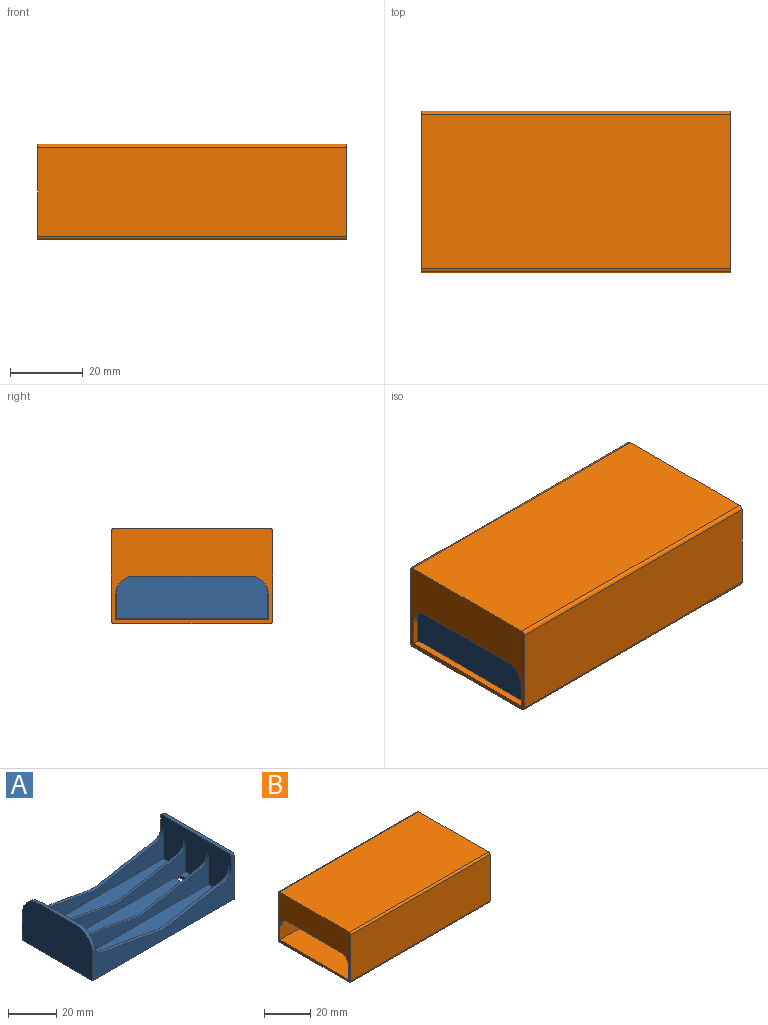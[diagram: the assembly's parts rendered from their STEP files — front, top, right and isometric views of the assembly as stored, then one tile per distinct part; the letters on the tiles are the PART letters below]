
ASSEMBLY  parts=2 mates=1
PART A: 45 faces, bbox 83.2x41.6x23.6 mm
  f0: plane 12x3.4mm, normal (0,0,1), area 40.8mm2, adj f6,f7,f11,f43
  f1: plane 83.2x22.6mm, normal (0,1,0), area 780.8mm2, adj f2,f11,f12,f17,f22,f23,f27,f30
  f2: plane 41.6x23.6mm, normal (-1,0,0), area 938.8mm2, adj f1,f3,f17,f18,f27,f28
  f3: plane 83.2x22.6mm, normal (0,-1,0), area 780.8mm2, adj f2,f11,f12,f17,f19,f26,f28,f29
  f4: plane 80x15mm, normal (0,1,0), area 595.9mm2, adj f9,f11,f16,f19,f26,f34,f35,f36
  f5: plane 80x15mm, normal (0,-1,0), area 595.9mm2, adj f9,f11,f16,f20,f24,f33,f37,f38
  f6: plane 80x16.6mm, normal (0,1,0), area 600.7mm2, adj f0,f9,f11,f15,f17,f20,f24,f33
  f7: plane 80x16.6mm, normal (0,-1,0), area 600.7mm2, adj f0,f9,f11,f15,f17,f21,f25,f32
  f8: plane 80x15mm, normal (0,1,0), area 595.9mm2, adj f9,f11,f14,f21,f25,f32,f39,f40
  f9: plane 40.68x22mm, normal (1,0,0), area 789.2mm2, adj f4,f5,f6,f7,f8,f10,f14,f15
  f10: plane 80x15mm, normal (0,-1,0), area 595.9mm2, adj f9,f11,f14,f22,f23,f31,f41,f42
  f11: plane 41.6x22mm, normal (-1,0,0), area 830.8mm2, adj f0,f1,f3,f4,f5,f6,f7,f8
  f12: plane 41.6x23.6mm, normal (1,0,0), area 981.3mm2, adj f1,f3,f13,f17,f29,f30
  f13: plane 39.6x1.6mm, normal (0,0,1), area 63.4mm2, adj f11,f12,f29,f30
  f14: plane 80x12mm, normal (0,0,1), area 960mm2, adj f8,f9,f10,f11
  f15: plane 73.6x12mm, normal (0,0,1), area 883.2mm2, adj f6,f7,f9,f44
  f16: plane 80x12mm, normal (0,0,1), area 960mm2, adj f4,f5,f9,f11
  f17: plane 83.2x41.6mm, normal (0,0,-1), area 3425.1mm2, adj f1,f2,f3,f6,f7,f12,f43,f44
  f18: plane 21.6x1.6mm, normal (0,0,1), area 34.6mm2, adj f2,f9,f27,f28
  f19: cylinder r=5mm len=4.94mm, axis (0,1,0), area 10.9mm2, adj f3,f4,f9,f28,f35
  f20: cylinder r=5mm len=4.94mm, axis (0,1,0), area 8.5mm2, adj f5,f6,f9,f37
  f21: cylinder r=5mm len=4.94mm, axis (0,1,0), area 8.5mm2, adj f7,f8,f9,f39
  f22: cylinder r=5mm len=4.94mm, axis (0,1,0), area 10.9mm2, adj f1,f9,f10,f27,f41
  f23: cylinder r=5mm len=4.94mm, axis (0,-1,0), area 11.3mm2, adj f1,f10,f11,f42
  f24: cylinder r=5mm len=4.94mm, axis (0,1,0), area 8.5mm2, adj f5,f6,f11,f38
  f25: cylinder r=5mm len=4.94mm, axis (0,1,0), area 8.5mm2, adj f7,f8,f11,f40
  f26: cylinder r=5mm len=4.94mm, axis (0,1,0), area 11.3mm2, adj f3,f4,f11,f36
  f27: cylinder r=10mm len=10mm, axis (1,0,0), area 26.1mm2, adj f1,f2,f9,f18,f22
  f28: cylinder r=10mm len=10mm, axis (-1,0,0), area 26.1mm2, adj f2,f3,f9,f18,f19
  f29: cylinder r=1mm len=1.6mm, axis (-1,0,0), area 2.5mm2, adj f3,f11,f12,f13
  f30: cylinder r=1mm len=1.6mm, axis (1,0,0), area 2.5mm2, adj f1,f11,f12,f13
  f31: cylinder r=21.24mm len=8.25mm, axis (0,-1,0), area 13.3mm2, adj f1,f10,f41,f42
  f32: cylinder r=21.24mm len=8.25mm, axis (0,-1,0), area 10mm2, adj f7,f8,f39,f40
  f33: cylinder r=21.24mm len=8.25mm, axis (0,-1,0), area 10mm2, adj f5,f6,f37,f38
  f34: cylinder r=21.24mm len=8.25mm, axis (0,-1,0), area 13.3mm2, adj f3,f4,f35,f36
  f35: cylinder r=800mm len=31.65mm, axis (0,-1,0), area 51.4mm2, adj f3,f4,f19,f34
  f36: cylinder r=800mm len=31.65mm, axis (0,1,0), area 51.4mm2, adj f3,f4,f26,f34
  f37: cylinder r=800mm len=31.65mm, axis (0,-1,0), area 38.6mm2, adj f5,f6,f20,f33
  f38: cylinder r=800mm len=31.65mm, axis (0,1,0), area 38.6mm2, adj f5,f6,f24,f33
  f39: cylinder r=800mm len=31.65mm, axis (0,-1,0), area 38.6mm2, adj f7,f8,f21,f32
  f40: cylinder r=800mm len=31.65mm, axis (0,1,0), area 38.6mm2, adj f7,f8,f25,f32
  f41: cylinder r=800mm len=31.65mm, axis (0,-1,0), area 51.4mm2, adj f1,f10,f22,f31
  f42: cylinder r=800mm len=31.65mm, axis (0,1,0), area 51.4mm2, adj f1,f10,f23,f31
  f43: plane 12x1.6mm, normal (-1,0,0), area 19.2mm2, adj f0,f6,f7,f17
  f44: plane 12x1.6mm, normal (1,0,0), area 19.2mm2, adj f6,f7,f15,f17
PART B: 37 faces, bbox 84.8x44.4x26.4 mm
  f0: plane 6x0.9mm, normal (1,0,0), area 5.4mm2, adj f17,f18,f20,f30
  f1: plane 84.8x42.4mm, normal (0,0,-1), area 3487.9mm2, adj f2,f4,f13,f14,f15,f16,f21,f22
  f2: plane 44.4x26.4mm, normal (-1,0,0), area 678mm2, adj f1,f3,f5,f6,f7,f9,f10,f11
  f3: plane 84.8x24mm, normal (0,-1,0), area 2014.8mm2, adj f2,f4,f8,f10,f12,f32
  f4: plane 44.4x26.4mm, normal (1,0,0), area 139.3mm2, adj f1,f3,f5,f6,f7,f10,f21,f24
  f5: plane 84.8x24.4mm, normal (0,1,0), area 2069.1mm2, adj f2,f4,f33,f36
  f6: plane 84.8x24mm, normal (0,1,0), area 2014.8mm2, adj f2,f4,f8,f10,f11,f32
  f7: plane 84.8x24.4mm, normal (0,-1,0), area 2069.1mm2, adj f2,f4,f34,f35
  f8: plane 42x17mm, normal (1,0,0), area 514.7mm2, adj f3,f6,f9,f11,f12,f32
  f9: plane 32x1.2mm, normal (0,0,-1), area 38.4mm2, adj f2,f8,f11,f12
  f10: plane 84.8x42mm, normal (0,0,1), area 3413.4mm2, adj f2,f3,f4,f6,f13,f14,f15,f16
  f11: cylinder r=5mm len=5mm, axis (1,0,0), area 9.4mm2, adj f2,f6,f8,f9
  f12: cylinder r=5mm len=5mm, axis (-1,0,0), area 9.4mm2, adj f2,f3,f8,f9
  f13: plane 8x1.2mm, normal (0,-1,0), area 9.5mm2, adj f1,f10,f22,f28,f29
  f14: plane 8x1.2mm, normal (0,1,0), area 9.5mm2, adj f1,f10,f23,f28,f29
  f15: plane 11x1.2mm, normal (0,-1,0), area 13.2mm2, adj f1,f10,f23,f24
  f16: plane 11x1.2mm, normal (0,1,0), area 13.2mm2, adj f1,f10,f21,f22
  f17: plane 3.28x0.9mm, normal (0,1,0), area 2.8mm2, adj f0,f19,f20,f25,f27
  f18: plane 3.28x0.9mm, normal (0,-1,0), area 2.8mm2, adj f0,f19,f20,f26,f27
  f19: plane 6x0.1mm, normal (-1,0,0), area 0.6mm2, adj f17,f18,f20,f27
  f20: plane 6x3mm, normal (0,0,1), area 18mm2, adj f0,f17,f18,f19
  f21: cylinder r=1mm len=1.2mm, axis (0,0,-1), area 1.9mm2, adj f1,f4,f10,f16
  f22: cylinder r=1mm len=2mm, axis (0,0,-1), area 3.8mm2, adj f1,f10,f13,f16
  f23: cylinder r=1mm len=2mm, axis (0,0,1), area 3.8mm2, adj f1,f10,f14,f15
  f24: cylinder r=1mm len=1.2mm, axis (0,0,-1), area 1.9mm2, adj f1,f4,f10,f15
  f25: cylinder r=0.5mm len=4.8mm, axis (1,0,0), area 3.1mm2, adj f10,f17,f27,f30
  f26: cylinder r=0.5mm len=4.8mm, axis (-1,0,0), area 3.1mm2, adj f10,f18,f27,f30
  f27: cylinder r=1.3mm len=7mm, axis (0,1,0), area 12.7mm2, adj f10,f17,f18,f19,f25,f26
  f28: plane 14x0.7mm, normal (1,0,0), area 9.8mm2, adj f1,f13,f14,f29
  f29: cylinder r=0.5mm len=14mm, axis (0,1,0), area 11mm2, adj f10,f13,f14,f28,f30
  f30: cylinder r=0.5mm len=7mm, axis (0,-1,0), area 5mm2, adj f0,f25,f26,f29
  f31: plane 84.8x42.4mm, normal (0,0,1), area 3595.5mm2, adj f2,f4,f33,f34
  f32: plane 83.6x42mm, normal (0,0,-1), area 3511.2mm2, adj f3,f4,f6,f8
  f33: cylinder r=1mm len=84.8mm, axis (1,0,0), area 133.2mm2, adj f2,f4,f5,f31
  f34: cylinder r=1mm len=84.8mm, axis (-1,0,0), area 133.2mm2, adj f2,f4,f7,f31
  f35: cylinder r=1mm len=84.8mm, axis (1,0,0), area 133.2mm2, adj f1,f2,f4,f7
  f36: cylinder r=1mm len=84.8mm, axis (-1,0,0), area 133.2mm2, adj f1,f2,f4,f5
PLACE A t=(-19.79,-11.07,10.41)mm
PLACE B t=(-18.86,-8.81,8.51)mm
MATE planar A.f12 <-> B.f4  axis (1,0,0) through (11.27,-6.77,20.61)mm
